# Revit family: Furniture_Chairs-Stools-Benches_Lekolar_Circum-laminate
name_source: partatom
category: Furniture
units: mm (PartAtom-declared; Revit-internal decimal feet)

## family parameters
Always vertical = No
Cut with Voids When Loaded = No
OmniClass Number = 23.40.20.00
OmniClass Title = General Furniture and Specialties
Room Calculation Point = No
Shared = No
Work Plane-Based = No

## types (1)
- Default
    BIMobject category = Chairs, Stools & Benches
    BIMobject category code = furniture-chairs-stools-benches
    BIMobject main category = Furniture
    BIMobject main category code = furniture
    BOSUseNativeGeometries = 1
    Brand url = https://www.lekolar.se
    Date of publishing = 10/23/1918
    Default Elevation = 0' - 0"
    Design country = Sweden
    Edition number = 1
    IFC Classification = Furniture
    Manufacturer country = Sweden
    Manufacturer name = Lekolar
    Masterformat 2014 Code = 12 52 13
    Masterformat 2014 Description = Chairs
    Material main = Wood
    Material secondary = Laminate
    NBS Reference Code = 31-12
    NBS Reference Description = Chairs, Seats And Bench Seating
    OmniClass Code = 23-21 21 33 13
    OmniClass Description = Commercial Restaurant Chairs
    Product Guid = 4cd2091e-0069-4f95-85aa-189487151659
    Product SKU = 81674
    Product data url = https://bimobject.com
    Product family = Circum
    Product group = Chair
    Product name = Circum laminate
    Product url = https://www.lekolar.se
    QR code = http://bimobject.com
    UNSPSC Code = 56
    Uniclass 1.4 Code = L8222
    Uniclass 1.4 Description = Chairs
    Uniclass 2.0 Code = PR-35-12-82
    Uniclass 2.0 Description = Stacking Chairs
    Uniclass 2015 Code = Pr_40_50_12
    Uniclass 2015 Name = Chairs, seats and benches
    Uniformat II Code = E2020
    Uniformat II Description = Movable Furnishings

## geometry (parser evidence)
native form markers: Sweep x1
no freeform markers — native parametric forms only
